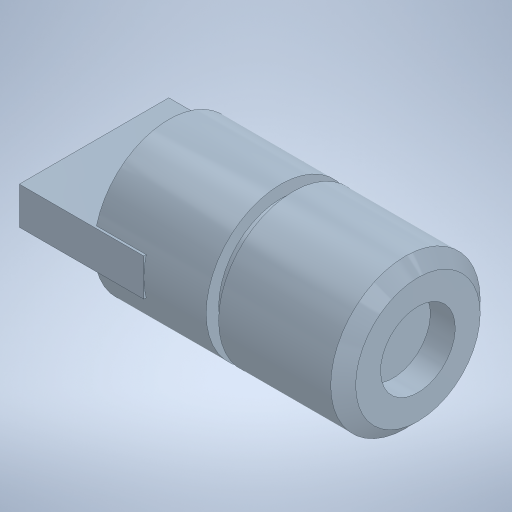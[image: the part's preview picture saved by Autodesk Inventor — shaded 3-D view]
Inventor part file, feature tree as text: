
AUTODESK INVENTOR PART (.ipt)
format: ipt  version: 2024.1 (Build 281209000, 209)  size: 260,608 bytes
history: native  units: in
note: dims shown in document units (in); Inventor stores cm internally (conversion verified against a paired STEP export)
features: chamfer x1, other x1
ambient origin geometry x8: Origin, YZ Plane, XZ Plane, XY Plane, X Axis, Y Axis, Z Axis, Center Point
bodies: Solid1 (feature_tree)
feature tree (2):
  chamfer  "Chamfer1"  Distance=0.0197in Angle=45.0deg
  other  "6mm 3v laser diode"
